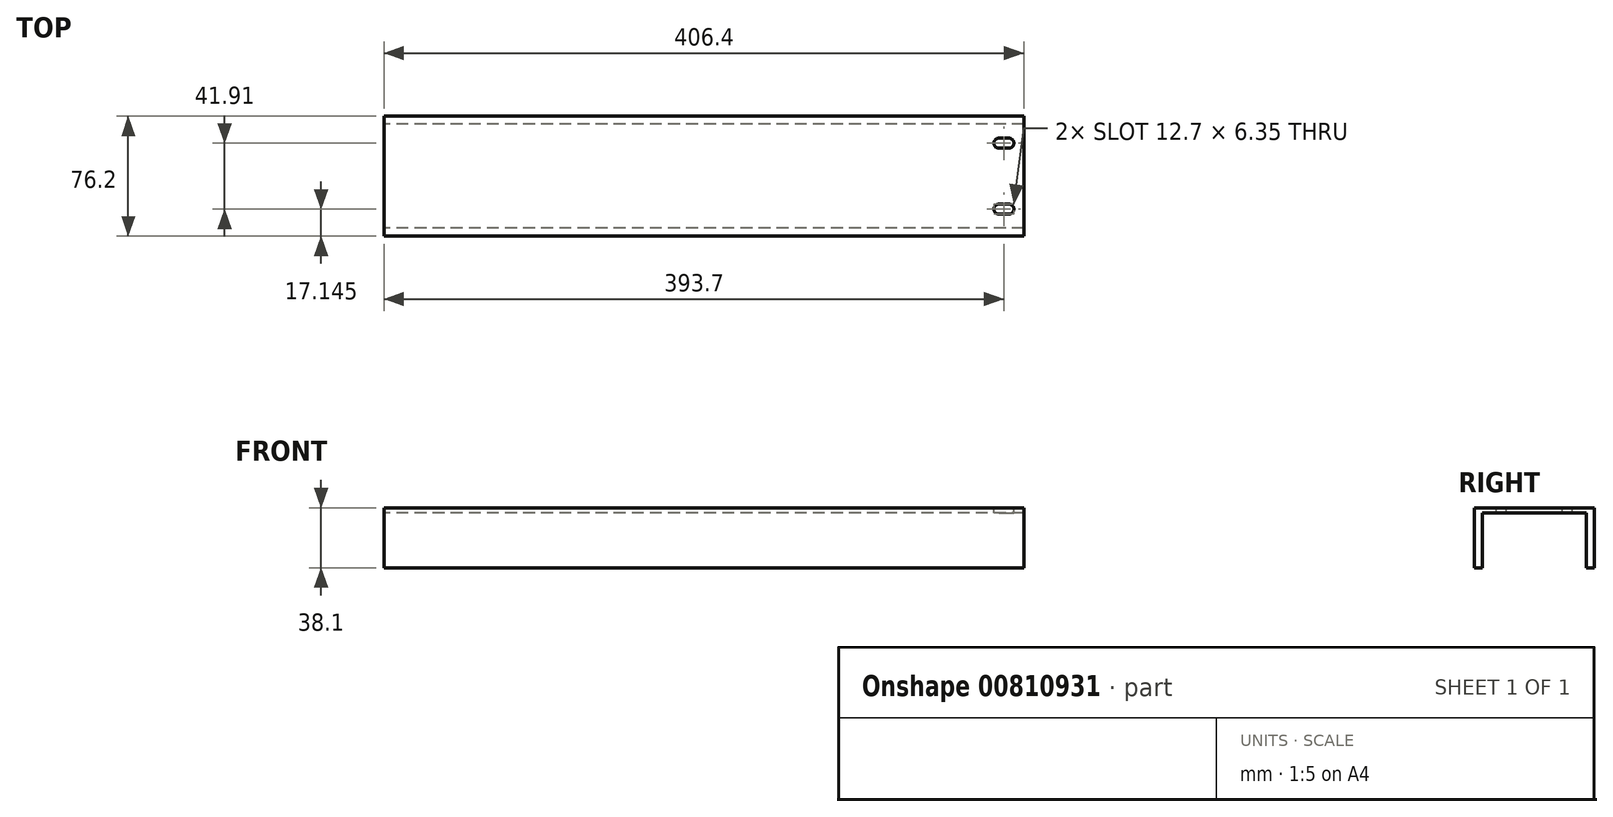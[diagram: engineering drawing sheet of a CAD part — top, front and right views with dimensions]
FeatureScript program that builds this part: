
annotation { "Feature Type Name" : "Feature", "Feature Type Description" : "" }
export const myFeature = defineFeature(function(context is Context, id is Id, definition is map)
    precondition{}
    {
        {
            var Q0;
            Q0=qCreatedBy(makeId("Right.planeOp"),FACE);
            var sketch = newSketch(context, id + "F0", { "sketchPlane" : qUnion([Q0])});
            skLineSegment(sketch, "E0.bottom", {"start": v(-38.1, 0) * mm, "end": v(38.1, 0) * mm});
            skLineSegment(sketch, "E0.top", {"start": v(-38.1, -38.1) * mm, "end": v(-33.02, -38.1) * mm});
            skLineSegment(sketch, "E0.left", {"start": v(-38.1, 0) * mm, "end": v(-38.1, -38.1) * mm});
            skLineSegment(sketch, "E0.right", {"start": v(38.1, 0) * mm, "end": v(38.1, -38.1) * mm});
            skLineSegment(sketch, "E1.bottom", {"start": v(-33.02, -3.3) * mm, "end": v(33.02, -3.3) * mm});
            skLineSegment(sketch, "E1.left", {"start": v(-33.02, -3.3) * mm, "end": v(-33.02, -38.1) * mm});
            skLineSegment(sketch, "E1.right", {"start": v(33.02, -3.3) * mm, "end": v(33.02, -38.1) * mm});
            skLineSegment(sketch, "E2.trimOffspring", {"start": v(33.02, -38.1) * mm, "end": v(38.1, -38.1) * mm});
            skSolve(sketch);
        }
        {
            var Q0;
            Q0 = qSketchRegion(id + "F0", true);
            extrude(context, id + "F1", {"entities" : qUnion([Q0]), "endBound" : BoundingType.SYMMETRIC, "depth" : 406.4 * mm, "offsetDistance" : 25.4 * mm});
        }
        {
            var Q0;
            Q0=makeQuery(id+"F1.opExtrude","SWEPT_FACE",FACE,{"disambiguationData":[OSD([sQuery(id+"F0.wireOp",EDGE,"E0.bottom")])]});
            var sketch = newSketch(context, id + "F2", { "sketchPlane" : qUnion([Q0])});
            skLineSegment(sketch, "E3.bottom", {"start": v(193.68, 17.78) * mm, "end": v(187.33, 17.78) * mm});
            skLineSegment(sketch, "E3.top", {"start": v(193.68, 24.13) * mm, "end": v(187.33, 24.13) * mm});
            skLineSegment(sketch, "E3.left", {"start": v(196.85, 20.95) * mm, "end": v(196.85, 20.95) * mm});
            skLineSegment(sketch, "E3.right", {"start": v(184.15, 20.95) * mm, "end": v(184.15, 20.95) * mm});
            skPoint(sketch, "E3.middle", {"position": v(190.5, 20.95) * mm});
            skPoint(sketch, "E4.visualSharp", {"position": v(196.85, 24.13) * mm});
            skArc(sketch, "E4.filletArc", {"start": v(196.85, 20.95) * mm, "mid": v(195.92, 23.2) * mm, "end": v(193.68, 24.13) * mm});
            skPoint(sketch, "E5.visualSharp", {"position": v(196.85, 17.78) * mm});
            skArc(sketch, "E5.filletArc", {"start": v(193.68, 17.78) * mm, "mid": v(195.92, 18.7) * mm, "end": v(196.85, 20.95) * mm});
            skPoint(sketch, "E6.visualSharp", {"position": v(184.15, 24.13) * mm});
            skArc(sketch, "E6.filletArc", {"start": v(187.33, 24.13) * mm, "mid": v(185.08, 23.2) * mm, "end": v(184.15, 20.95) * mm});
            skPoint(sketch, "E7.visualSharp", {"position": v(184.15, 17.78) * mm});
            skArc(sketch, "E7.filletArc", {"start": v(184.15, 20.95) * mm, "mid": v(185.08, 18.7) * mm, "end": v(187.33, 17.78) * mm});
            skArc(sketch, "E8.MirrorCS", {"start": v(193.68, -17.78) * mm, "mid": v(195.92, -18.7) * mm, "end": v(196.85, -20.95) * mm});
            skArc(sketch, "E9.MirrorCS", {"start": v(184.15, -20.95) * mm, "mid": v(185.08, -18.7) * mm, "end": v(187.33, -17.78) * mm});
            skArc(sketch, "E10.MirrorCS", {"start": v(187.33, -24.13) * mm, "mid": v(185.08, -23.2) * mm, "end": v(184.15, -20.95) * mm});
            skArc(sketch, "E11.MirrorCS", {"start": v(196.85, -20.95) * mm, "mid": v(195.92, -23.2) * mm, "end": v(193.68, -24.13) * mm});
            skLineSegment(sketch, "E12.MirrorCS", {"start": v(193.68, -17.78) * mm, "end": v(187.33, -17.78) * mm});
            skLineSegment(sketch, "E13.MirrorCS", {"start": v(193.68, -24.13) * mm, "end": v(187.33, -24.13) * mm});
            skPoint(sketch, "E14.MirrorP", {"position": v(190.5, -20.95) * mm});
            skPoint(sketch, "E15.MirrorP", {"position": v(196.85, -17.78) * mm});
            skPoint(sketch, "E16.MirrorP", {"position": v(184.15, -24.13) * mm});
            skPoint(sketch, "E17.MirrorP", {"position": v(196.85, -24.13) * mm});
            skPoint(sketch, "E18.MirrorP", {"position": v(184.15, -17.78) * mm});
            skSolve(sketch);
        }
        {
            var Q0;
            Q0 = qSketchRegion(id + "F2", true);
            extrude(context, id + "F3", {"entities" : qUnion([Q0]), "operationType" : NewBodyOperationType.REMOVE, "endBound" : BoundingType.UP_TO_NEXT, "oppositeDirection" : true, "depth" : 25.4 * mm, "offsetDistance" : 25.4 * mm});
        }
    });
